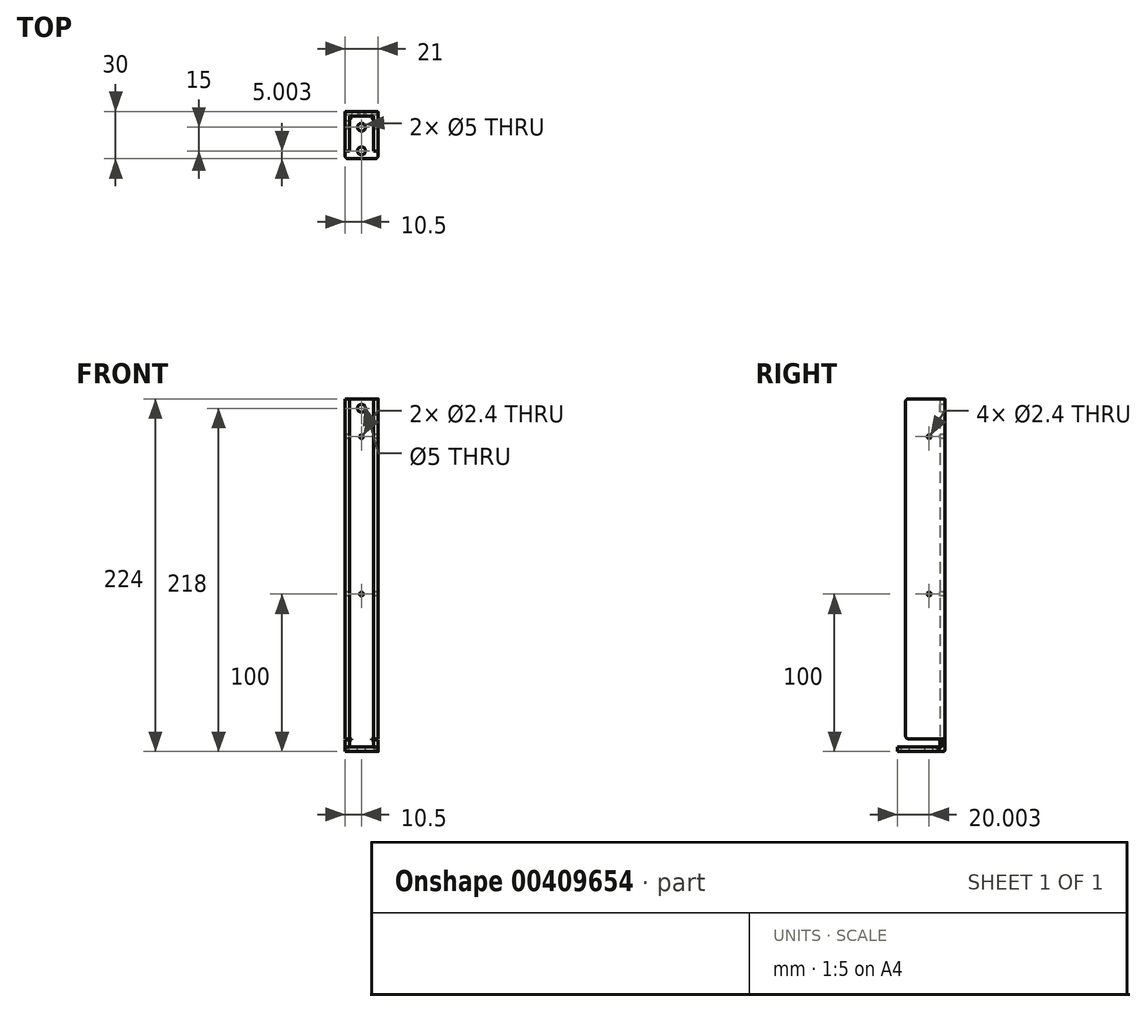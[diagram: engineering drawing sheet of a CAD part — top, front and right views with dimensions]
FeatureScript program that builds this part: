
annotation { "Feature Type Name" : "Feature", "Feature Type Description" : "" }
export const myFeature = defineFeature(function(context is Context, id is Id, definition is map)
    precondition{}
    {
        {
            var Q0;
            Q0=qCreatedBy(makeId("Right.planeOp"),FACE);
            var sketch = newSketch(context, id + "F0", { "sketchPlane" : qUnion([Q0])});
            skLineSegment(sketch, "E0", {"start": v(-7.6, 0) * mm, "end": v(22.4, 0) * mm});
            skLineSegment(sketch, "E1", {"start": v(22.4, 0) * mm, "end": v(22.4, 224) * mm});
            skLineSegment(sketch, "E2", {"start": v(22.4, 224) * mm, "end": v(19.4, 224) * mm});
            skLineSegment(sketch, "E3", {"start": v(19.4, 224) * mm, "end": v(19.4, 3) * mm});
            skLineSegment(sketch, "E4", {"start": v(19.4, 3) * mm, "end": v(-7.6, 3) * mm});
            skLineSegment(sketch, "E5", {"start": v(-7.6, 3) * mm, "end": v(-7.6, 0) * mm});
            skSolve(sketch);
        }
        {
            var Q0;
            Q0=qSketchRegion(id+"F0",true);
            extrude(context, id + "F1", {"entities" : qUnion([Q0]), "depth" : 15 * mm});
        }
        {
            var Q0;
            Q0=makeQuery(id+"F1.opExtrude","SWEPT_FACE",FACE,{"disambiguationData":[OSD([sQuery(id+"F0.wireOp",EDGE,"E1")])]});
            var sketch = newSketch(context, id + "F2", { "sketchPlane" : qUnion([Q0])});
            skLineSegment(sketch, "E6.bottom", {"start": v(0, 8) * mm, "end": v(3, 8) * mm});
            skLineSegment(sketch, "E6.top", {"start": v(0, 224) * mm, "end": v(3, 224) * mm});
            skLineSegment(sketch, "E6.left", {"start": v(0, 8) * mm, "end": v(0, 224) * mm});
            skLineSegment(sketch, "E6.right", {"start": v(3, 8) * mm, "end": v(3, 224) * mm});
            skLineSegment(sketch, "E7.bottom", {"start": v(-15, 224) * mm, "end": v(-18, 224) * mm});
            skLineSegment(sketch, "E7.top", {"start": v(-15, 8) * mm, "end": v(-18, 8) * mm});
            skLineSegment(sketch, "E7.left", {"start": v(-15, 224) * mm, "end": v(-15, 8) * mm});
            skLineSegment(sketch, "E7.right", {"start": v(-18, 224) * mm, "end": v(-18, 8) * mm});
            skSolve(sketch);
        }
        {
            var Q0;
            Q0=qSketchRegion(id+"F2",true);
            extrude(context, id + "F3", {"entities" : qUnion([Q0]), "operationType" : NewBodyOperationType.ADD, "oppositeDirection" : true, "depth" : 25 * mm});
        }
        {
            var Q0;
            Q0=makeQuery(id+"F1.opExtrude","SWEPT_FACE",FACE,{"disambiguationData":[OSD([sQuery(id+"F0.wireOp",EDGE,"E4")])]});
            var sketch = newSketch(context, id + "F4", { "sketchPlane" : qUnion([Q0])});
            skCircle(sketch, "E8", {"center": v(7.5, -2.6) * mm, "radius": 2.5 * mm});
            skCircle(sketch, "E9", {"center": v(7.5, 12.4) * mm, "radius": 2.5 * mm});
            skSolve(sketch);
        }
        {
            var Q0;
            Q0=qSketchRegion(id+"F4",true);
            extrude(context, id + "F5", {"entities" : qUnion([Q0]), "operationType" : NewBodyOperationType.REMOVE, "oppositeDirection" : true, "depth" : 3 * mm});
        }
        {
            var Q0;
            Q0=makeQuery(id+"F1.opExtrude","SWEPT_FACE",FACE,{"disambiguationData":[OSD([sQuery(id+"F0.wireOp",EDGE,"E3")])]});
            var sketch = newSketch(context, id + "F6", { "sketchPlane" : qUnion([Q0])});
            skLineSegment(sketch, "E10.bottom", {"start": v(0, 8) * mm, "end": v(1, 8) * mm});
            skLineSegment(sketch, "E10.top", {"start": v(0, 7.5) * mm, "end": v(1, 7.5) * mm});
            skLineSegment(sketch, "E10.left", {"start": v(0, 8) * mm, "end": v(0, 7.5) * mm});
            skLineSegment(sketch, "E10.right", {"start": v(1, 8) * mm, "end": v(1, 7.5) * mm});
            skLineSegment(sketch, "E11.bottom", {"start": v(15, 8) * mm, "end": v(14, 8) * mm});
            skLineSegment(sketch, "E11.top", {"start": v(15, 7.5) * mm, "end": v(14, 7.5) * mm});
            skLineSegment(sketch, "E11.left", {"start": v(15, 8) * mm, "end": v(15, 7.5) * mm});
            skLineSegment(sketch, "E11.right", {"start": v(14, 8) * mm, "end": v(14, 7.5) * mm});
            skSolve(sketch);
        }
        {
            var Q0;
            Q0=qSketchRegion(id+"F6",true);
            extrude(context, id + "F7", {"entities" : qUnion([Q0]), "operationType" : NewBodyOperationType.REMOVE, "oppositeDirection" : true, "depth" : 3 * mm});
        }
        {
            var Q0;
            Q0=makeQuery(id+"F1.opExtrude","SWEPT_EDGE",EDGE,{"disambiguationData":[OSD([sQuery(id+"F0.wireOp",EDGE,"E3"),sQuery(id+"F0.wireOp",EDGE,"E4")])]});
            var Q1;
            Q1=makeQuery(id+"F1.opExtrude","SWEPT_EDGE",EDGE,{"disambiguationData":[OSD([sQuery(id+"F0.wireOp",EDGE,"E0"),sQuery(id+"F0.wireOp",EDGE,"E1")])]});
            var Q2;
            {var subQ0=sQuery(id+"F0.wireOp",EDGE,"E3");Q2=makeQuery(id+"F3.boolean.opBoolean","SPLIT",EDGE,{"disambiguationData":[topologyDisambiguationEdgeConnected([makeQuery(id+"F3.opExtrude","SWEPT_FACE",FACE,{"disambiguationData":[OSD([sQuery(id+"F2.wireOp",EDGE,"E6.left")])]})])],"derivedFrom":makeQuery(id+"F1.opExtrude","CAP_EDGE",EDGE,{"disambiguationData":[OSD([subQ0])],"isStart":true})});}
            var Q3;
            Q3=makeQuery(id+"F3.opExtrude","CAP_EDGE",EDGE,{"disambiguationData":[OSD([sQuery(id+"F2.wireOp",EDGE,"E6.right")])],"isStart":true});
            var Q4;
            Q4=makeQuery(id+"F3.opExtrude","CAP_EDGE",EDGE,{"disambiguationData":[OSD([sQuery(id+"F2.wireOp",EDGE,"E7.right")])],"isStart":true});
            var Q5;
            {var subQ0=sQuery(id+"F0.wireOp",EDGE,"E3");Q5=makeQuery(id+"F3.boolean.opBoolean","SPLIT",EDGE,{"disambiguationData":[topologyDisambiguationEdgeConnected([makeQuery(id+"F3.opExtrude","SWEPT_FACE",FACE,{"disambiguationData":[OSD([sQuery(id+"F2.wireOp",EDGE,"E7.left")])]})])],"derivedFrom":makeQuery(id+"F1.opExtrude","CAP_EDGE",EDGE,{"disambiguationData":[OSD([subQ0])],"isStart":false})});}
            fillet(context, id + "F8", {"entities" : qUnion([Q0, Q1, Q2, Q3, Q4, Q5]), "radius" : 1 * mm, "tangentPropagation" : true, "allowEdgeOverflow" : false});
        }
        {
            var Q0;
            Q0=makeQuery(id+"F1.opExtrude","SWEPT_FACE",FACE,{"disambiguationData":[OSD([sQuery(id+"F0.wireOp",EDGE,"E3")])]});
            var sketch = newSketch(context, id + "F9", { "sketchPlane" : qUnion([Q0])});
            skCircle(sketch, "E12", {"center": v(7.5, 218) * mm, "radius": 2.5 * mm});
            skPoint(sketch, "E12.centerSnap0", {"position": v(7.5, 224) * mm});
            skCircle(sketch, "E13", {"center": v(7.5, 100) * mm, "radius": 1.2 * mm});
            skPoint(sketch, "E13.centerSnap0", {"position": v(7.5, 4) * mm});
            skCircle(sketch, "E14", {"center": v(7.5, 200) * mm, "radius": 1.2 * mm});
            skSolve(sketch);
        }
        {
            var Q0;
            Q0=qSketchRegion(id+"F9",true);
            extrude(context, id + "F10", {"entities" : qUnion([Q0]), "operationType" : NewBodyOperationType.REMOVE, "oppositeDirection" : true, "depth" : 3 * mm});
        }
        {
            var Q0;
            Q0=makeQuery(id+"F3.opExtrude","SWEPT_FACE",FACE,{"disambiguationData":[OSD([sQuery(id+"F2.wireOp",EDGE,"E6.right")])]});
            var sketch = newSketch(context, id + "F11", { "sketchPlane" : qUnion([Q0])});
            skCircle(sketch, "E15", {"center": v(-12.4, 200) * mm, "radius": 1.2 * mm});
            skCircle(sketch, "E16", {"center": v(-12.4, 100) * mm, "radius": 1.2 * mm});
            skSolve(sketch);
        }
        {
            var Q0;
            Q0=qSketchRegion(id+"F11",true);
            extrude(context, id + "F12", {"entities" : qUnion([Q0]), "operationType" : NewBodyOperationType.REMOVE, "oppositeDirection" : true, "depth" : 34.2 * mm});
        }
        {
            var Q0;
            Q0=makeQuery(id+"F1.opExtrude","CAP_FACE",FACE,{"disambiguationData":[OSD([sQuery(id+"F0.wireOp",EDGE,"E0"),sQuery(id+"F0.wireOp",EDGE,"E1"),sQuery(id+"F0.wireOp",EDGE,"E2"),sQuery(id+"F0.wireOp",EDGE,"E3"),sQuery(id+"F0.wireOp",EDGE,"E4"),sQuery(id+"F0.wireOp",EDGE,"E5")])],"isStart":true});
            var Q1;
            Q1=makeQuery(id+"F1.opExtrude","CAP_FACE",FACE,{"disambiguationData":[OSD([sQuery(id+"F0.wireOp",EDGE,"E0"),sQuery(id+"F0.wireOp",EDGE,"E1"),sQuery(id+"F0.wireOp",EDGE,"E2"),sQuery(id+"F0.wireOp",EDGE,"E3"),sQuery(id+"F0.wireOp",EDGE,"E4"),sQuery(id+"F0.wireOp",EDGE,"E5")])],"isStart":false});
            extrude(context, id + "F13", {"entities" : qUnion([Q0, Q1]), "operationType" : NewBodyOperationType.ADD, "endBound" : BoundingType.SYMMETRIC, "depth" : 6 * mm});
        }
        {
            var Q0;
            {var subQ0=sQuery(id+"F0.wireOp",EDGE,"E5");Q0=makeQuery(id+"F13.opExtrude","CAP_EDGE",EDGE,{"disambiguationData":[OSD([subQ0]),TDD([makeQuery(id+"F1.opExtrude","CAP_EDGE",EDGE,{"disambiguationData":[OSD([subQ0])],"isStart":true})])],"isStart":false});}
            var Q1;
            {var subQ0=sQuery(id+"F0.wireOp",EDGE,"E5");Q1=makeQuery(id+"F13.opExtrude","CAP_EDGE",EDGE,{"disambiguationData":[OSD([subQ0]),TDD([makeQuery(id+"F1.opExtrude","CAP_EDGE",EDGE,{"disambiguationData":[OSD([subQ0])],"isStart":false})])],"isStart":true});}
            var Q2;
            Q2=makeQuery(id+"F3.opExtrude","CAP_EDGE",EDGE,{"disambiguationData":[OSD([sQuery(id+"F2.wireOp",EDGE,"E6.bottom")])],"isStart":false});
            var Q3;
            Q3=makeQuery(id+"F3.opExtrude","CAP_EDGE",EDGE,{"disambiguationData":[OSD([sQuery(id+"F2.wireOp",EDGE,"E7.top")])],"isStart":false});
            var Q4;
            Q4=makeQuery(id+"F3.opExtrude","CAP_EDGE",EDGE,{"disambiguationData":[OSD([sQuery(id+"F2.wireOp",EDGE,"E6.top")])],"isStart":false});
            var Q5;
            Q5=makeQuery(id+"F3.opExtrude","CAP_EDGE",EDGE,{"disambiguationData":[OSD([sQuery(id+"F2.wireOp",EDGE,"E7.bottom")])],"isStart":false});
            fillet(context, id + "F14", {"entities" : qUnion([Q0, Q1, Q2, Q3, Q4, Q5]), "radius" : 2 * mm, "tangentPropagation" : true, "allowEdgeOverflow" : false});
        }
    });
